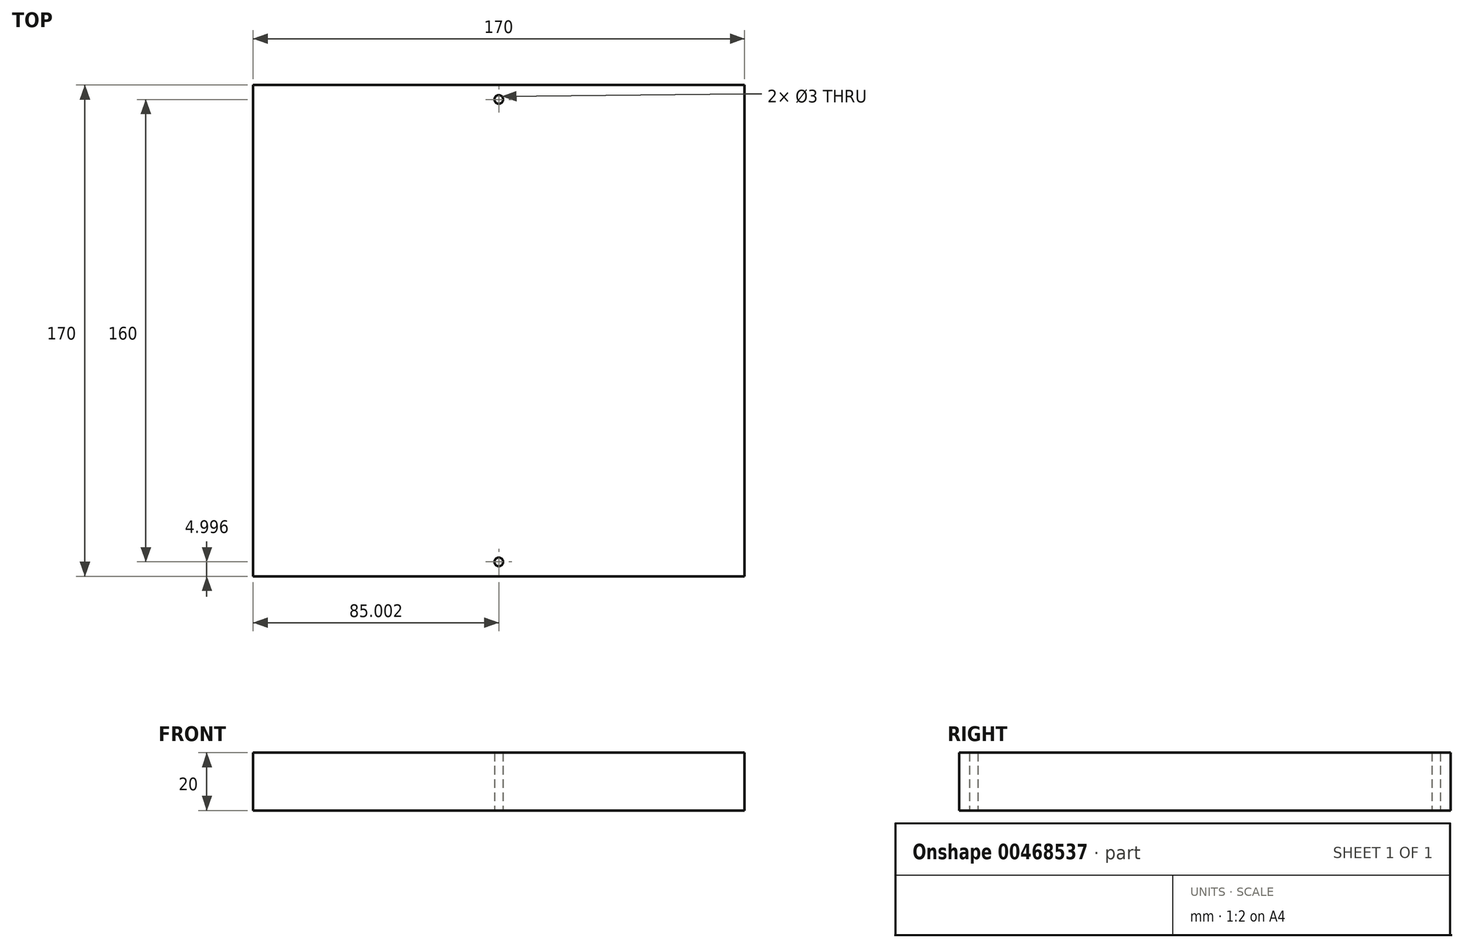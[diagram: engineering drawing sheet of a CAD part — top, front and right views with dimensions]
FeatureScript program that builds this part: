
annotation { "Feature Type Name" : "Feature", "Feature Type Description" : "" }
export const myFeature = defineFeature(function(context is Context, id is Id, definition is map)
    precondition{}
    {
        {
            var Q0;
            Q0=qCreatedBy(makeId("Top.planeOp"),FACE);
            var sketch = newSketch(context, id + "F0", { "sketchPlane" : qUnion([Q0])});
            skLineSegment(sketch, "E0.bottom", {"start": v(-86.17, 90.7) * mm, "end": v(83.83, 90.7) * mm});
            skLineSegment(sketch, "E0.top", {"start": v(-86.17, -79.3) * mm, "end": v(83.83, -79.3) * mm});
            skLineSegment(sketch, "E0.left", {"start": v(-86.17, 90.7) * mm, "end": v(-86.17, -79.3) * mm});
            skLineSegment(sketch, "E0.right", {"start": v(83.83, 90.7) * mm, "end": v(83.83, -79.3) * mm});
            skPoint(sketch, "E1", {"position": v(-1.17, 90.7) * mm});
            skLineSegment(sketch, "E2", {"start": v(-1.17, 90.7) * mm, "end": v(-1.17, 85.7) * mm, "construction": true});
            skCircle(sketch, "E3", {"center": v(-1.17, 85.7) * mm, "radius": 1.5 * mm});
            skPoint(sketch, "E4", {"position": v(-1.17, -79.3) * mm});
            skCircle(sketch, "E5", {"center": v(-1.17, -74.3) * mm, "radius": 1.5 * mm});
            skSolve(sketch);
        }
        {
            var Q0;
            Q0=makeQuery(id+"F0.imprint","IMPRINT",FACE,{"disambiguationData":[TD([[makeQuery(id+"F0.imprint","IMPRINT",EDGE,{"derivedFrom":sQuery(id+"F0.wireOp",EDGE,"E0.bottom")}),-1.0]])]});
            extrude(context, id + "F1", {"entities" : qUnion([Q0]), "depth" : 20 * mm, "offsetDistance" : 25 * mm});
        }
    });
